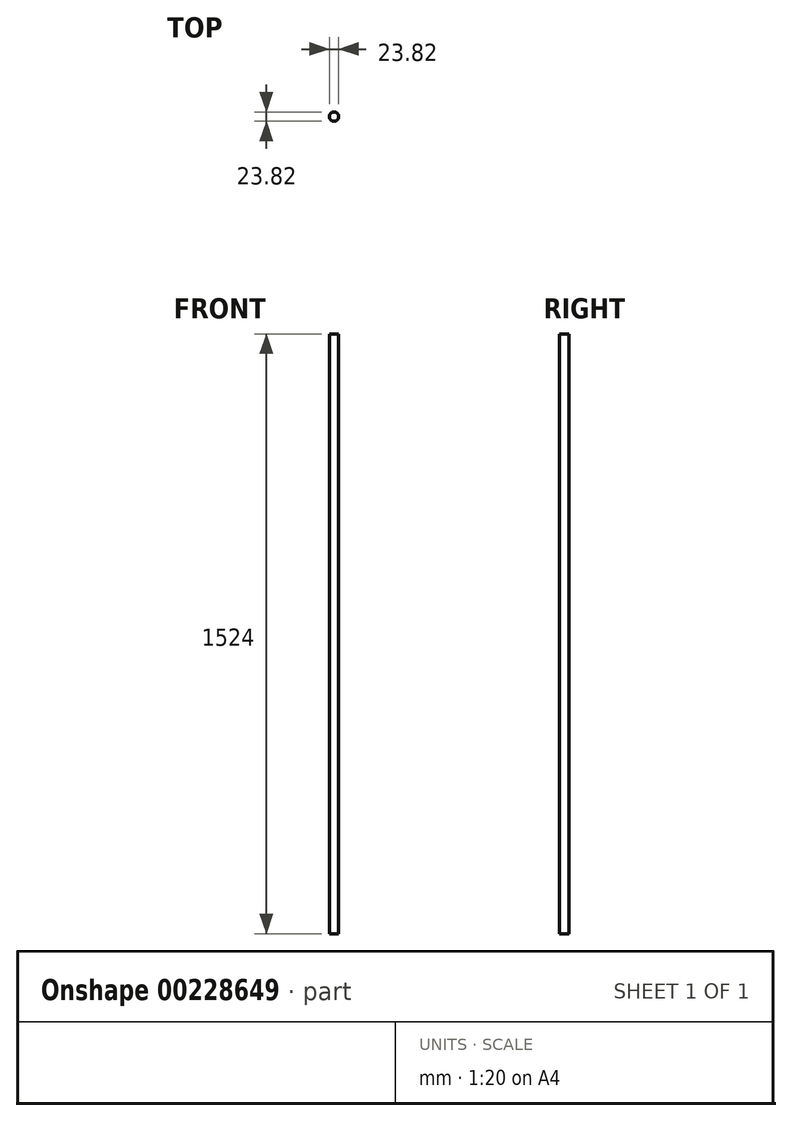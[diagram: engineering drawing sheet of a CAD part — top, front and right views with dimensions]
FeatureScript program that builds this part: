
annotation { "Feature Type Name" : "Feature", "Feature Type Description" : "" }
export const myFeature = defineFeature(function(context is Context, id is Id, definition is map)
    precondition{}
    {
        {
            var Q0;
            Q0=qCreatedBy(makeId("Top.planeOp"),FACE);
            var sketch = newSketch(context, id + "F0", { "sketchPlane" : qUnion([Q0])});
            skCircle(sketch, "E0", {"center": v(0, 0) * mm, "radius": 11.9 * mm});
            skSolve(sketch);
        }
        {
            var Q0;
            Q0 = qSketchRegion(id + "F0", true);
            extrude(context, id + "F1", {"entities" : qUnion([Q0]), "oppositeDirection" : true, "depth" : 1524 * mm});
        }
    });
